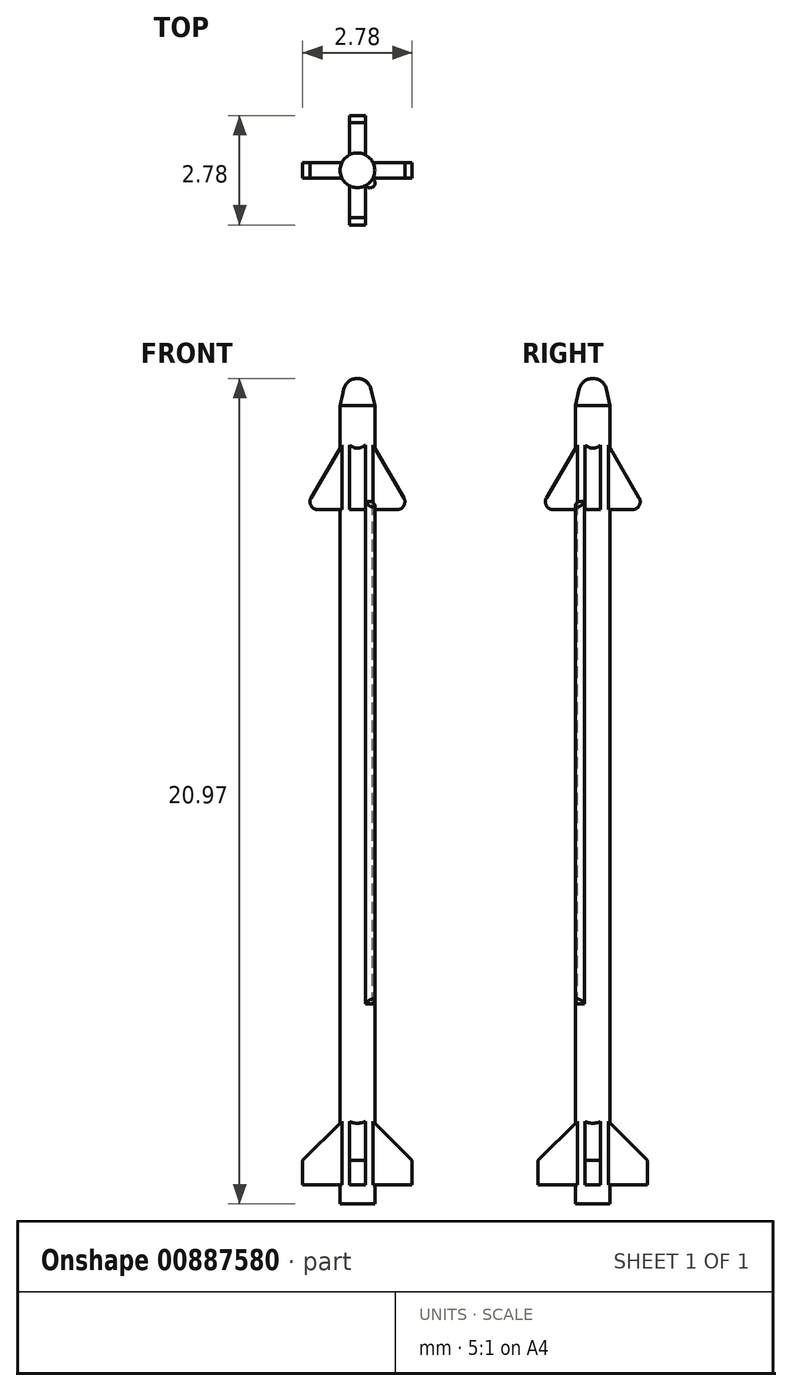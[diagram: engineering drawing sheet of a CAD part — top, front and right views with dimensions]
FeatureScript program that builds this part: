
annotation { "Feature Type Name" : "Feature", "Feature Type Description" : "" }
export const myFeature = defineFeature(function(context is Context, id is Id, definition is map)
    precondition{}
    {
        {
            var Q0;
            Q0=qCreatedBy(makeId("Front.planeOp"),FACE);
            var sketch = newSketch(context, id + "F0", { "sketchPlane" : qUnion([Q0])});
            skLineSegment(sketch, "E0", {"start": v(0, 0) * mm, "end": v(0, 20.97) * mm});
            skLineSegment(sketch, "E1", {"start": v(0.44, 20.28) * mm, "end": v(0.44, 0) * mm});
            skLineSegment(sketch, "E2", {"start": v(0.44, 0) * mm, "end": v(0, 0) * mm});
            skLineSegment(sketch, "E3", {"start": v(0, 20.97) * mm, "end": v(1.85, 20.97) * mm, "construction": true});
            skLineSegment(sketch, "E4", {"start": v(0.44, 20.28) * mm, "end": v(0.35, 20.7) * mm});
            skArc(sketch, "E5", {"start": v(0.35, 20.7) * mm, "mid": v(0.22, 20.9) * mm, "end": v(0, 20.97) * mm});
            skSolve(sketch);
        }
        {
            var Q0;
            Q0=qSketchRegion(id+"F0",true);
            var Q1;
            Q1=sQuery(id+"F0.wireOp",EDGE,"E0");
            revolve(context, id + "F1", {"surfaceOperationType" : NewSurfaceOperationType.NEW, "entities" : qUnion([Q0]), "axis" : qUnion([Q1]), "revolveType" : RevolveType.FULL});
        }
        {
            var Q0;
            Q0=qCreatedBy(makeId("Front.planeOp"),FACE);
            var sketch = newSketch(context, id + "F2", { "sketchPlane" : qUnion([Q0])});
            skLineSegment(sketch, "E6", {"start": v(0.25, 2.24) * mm, "end": v(-0.25, 2.24) * mm});
            skLineSegment(sketch, "E7", {"start": v(-1.39, 1.11) * mm, "end": v(-0.25, 2.24) * mm});
            skLineSegment(sketch, "E8", {"start": v(-1.39, 1.11) * mm, "end": v(-1.39, 0.49) * mm});
            skLineSegment(sketch, "E9", {"start": v(1.39, 0.49) * mm, "end": v(1.39, 1.11) * mm});
            skLineSegment(sketch, "E10", {"start": v(0.25, 2.24) * mm, "end": v(1.39, 1.11) * mm});
            skLineSegment(sketch, "E11", {"start": v(0, 0) * mm, "end": v(0, 2.24) * mm, "construction": true});
            skLineSegment(sketch, "E12", {"start": v(-0.44, 0.8) * mm, "end": v(-0.44, 4.16) * mm, "construction": true});
            skLineSegment(sketch, "E13.0", {"start": v(0.44, 20.28) * mm, "end": v(-0.44, 20.28) * mm});
            skLineSegment(sketch, "E14", {"start": v(0, 0) * mm, "end": v(0, 0.49) * mm, "construction": true});
            skLineSegment(sketch, "E15.0", {"start": v(0.44, 0) * mm, "end": v(-0.44, 0) * mm});
            skLineSegment(sketch, "E16", {"start": v(-1.35, 17.64) * mm, "end": v(1.35, 17.64) * mm});
            skLineSegment(sketch, "E17", {"start": v(-1.35, 17.64) * mm, "end": v(-0.25, 19.53) * mm});
            skLineSegment(sketch, "E18", {"start": v(-0.25, 19.53) * mm, "end": v(0.25, 19.53) * mm});
            skLineSegment(sketch, "E19", {"start": v(0.25, 19.53) * mm, "end": v(1.35, 17.64) * mm});
            skLineSegment(sketch, "E20", {"start": v(0, 19.53) * mm, "end": v(0, 17.64) * mm, "construction": true});
            skLineSegment(sketch, "E21", {"start": v(-1.39, 0.49) * mm, "end": v(1.39, 0.49) * mm});
            skPoint(sketch, "E22", {"position": v(-0.44, 2.05) * mm});
            skLineSegment(sketch, "E23", {"start": v(-0.44, 20.28) * mm, "end": v(-0.44, 16.68) * mm, "construction": true});
            skPoint(sketch, "E24", {"position": v(-0.44, 19.2) * mm});
            skSolve(sketch);
        }
        {
            var Q0;
            Q0=qSketchRegion(id+"F2",true);
            extrude(context, id + "F3", {"entities" : qUnion([Q0]), "operationType" : NewBodyOperationType.ADD, "depth" : .4 * mm, "offsetDistance" : 25 * mm, "symmetric" : true});
        }
        {
            var Q0;
            Q0=makeQuery(id+"F3.opExtrude","SWEPT_EDGE",EDGE,{"disambiguationData":[OSD([sQuery(id+"F2.wireOp",EDGE,"IMAepUiN-4dFO-ApNK-NmcL-y1ty9Cx0r7KA"),sQuery(id+"F2.wireOp",EDGE,"E16")])]});
            var Q1;
            Q1=makeQuery(id+"F3.opExtrude","SWEPT_EDGE",EDGE,{"disambiguationData":[OSD([sQuery(id+"F2.wireOp",EDGE,"Mpjs0J2t-wY67-a0AX-eRwJ-QufGG5zaKpuO"),sQuery(id+"F2.wireOp",EDGE,"E16")])]});
            fillet(context, id + "F4", {"entities" : qUnion([Q0, Q1]), "radius" : .2 * mm, "tangentPropagation" : true, "allowEdgeOverflow" : false});
        }
        {
            var Q0;
            Q0=makeQuery(id+"F1.opRevolve","SWEPT_BODY",BODY,{"disambiguationData":[OSD([sQuery(id+"F0.wireOp",EDGE,"E0"),sQuery(id+"F0.wireOp",EDGE,"E1"),sQuery(id+"F0.wireOp",EDGE,"E2"),sQuery(id+"F0.wireOp",EDGE,"m1K1lCZm-MTc8-Btmt-IA6e-LtdyprMEJuD3")])]});
            var Q1;
            Q1=makeQuery(id+"F1.opRevolve","SWEPT_FACE",FACE,{"disambiguationData":[OSD([sQuery(id+"F0.wireOp",EDGE,"E1")])]});
            circularPattern(context, id + "F5", {"entities" : qUnion([Q0]), "axis" : qUnion([Q1]), "angle" : 360 * degree, "instanceCount" : 4, "equalSpace" : true, "computeTransformsWithoutBuiltin" : true});
        }
        {
            var Q0;
            {var subQ2=sQuery(id+"F2.wireOp",EDGE,"E17");var subQ3=sQuery(id+"F2.wireOp",EDGE,"E16");Q0=makeQuery(id+"F5.opPattern","COPY",FACE,{"derivedFrom":makeQuery(id+"F3.boolean.opBoolean","SPLIT",FACE,{"disambiguationData":[TD([makeQuery(id+"F3.opExtrude","SWEPT_FACE",FACE,{"disambiguationData":[OSD([subQ2])]})])],"derivedFrom":makeQuery(id+"F3.opExtrude","SWEPT_FACE",FACE,{"disambiguationData":[OSD([subQ3])]})}),"instanceName":"1"});}
            var sketch = newSketch(context, id + "F6", { "sketchPlane" : qUnion([Q0])});
            skCircle(sketch, "E25.0.0", {"center": v(0, 0) * mm, "radius": 0.44 * mm});
            skArc(sketch, "E26", {"start": v(0.41, 0.23) * mm, "mid": v(0.41, 0.41) * mm, "end": v(0.23, 0.41) * mm});
            skLineSegment(sketch, "E27", {"start": v(0.23, 0.41) * mm, "end": v(0.2, 0.38) * mm});
            skLineSegment(sketch, "E28", {"start": v(0.2, 0.38) * mm, "end": v(0.38, 0.2) * mm});
            skLineSegment(sketch, "E29", {"start": v(0.38, 0.2) * mm, "end": v(0.41, 0.23) * mm});
            skLineSegment(sketch, "E30", {"start": v(0.3, 0.3) * mm, "end": v(0, 0) * mm, "construction": true});
            skLineSegment(sketch, "E31", {"start": v(0, 0) * mm, "end": v(0.17, 0) * mm, "construction": true});
            skSolve(sketch);
        }
        {
            var Q0;
            Q0 = qSketchRegion(id + "F6", true);
            extrude(context, id + "F7", {"entities" : qUnion([Q0]), "operationType" : NewBodyOperationType.ADD, "depth" : (1780 / 144) * mm, "offsetDistance" : 25 * mm});
        }
        {
            var Q0;
            {var subQ0=makeQuery(id+"F1.opRevolve","SWEPT_FACE",FACE,{"disambiguationData":[OSD([sQuery(id+"F0.wireOp",EDGE,"E1")])]});Q0=makeQuery(id+"F7.boolean.opBoolean","INTERSECT",EDGE,{"derivedFrom":[subQ0,makeQuery(id+"F5.opPattern","COPY",FACE,{"derivedFrom":subQ0,"instanceName":"1"}),makeQuery(id+"F5.opPattern","COPY",FACE,{"derivedFrom":subQ0,"instanceName":"2"}),makeQuery(id+"F5.opPattern","COPY",FACE,{"derivedFrom":subQ0,"instanceName":"3"}),makeQuery(id+"F7.opExtrude","CAP_FACE",FACE,{"disambiguationData":[OSD([sQuery(id+"F6.wireOp",EDGE,"E25.0.0"),sQuery(id+"F6.wireOp",EDGE,"E26"),sQuery(id+"F6.wireOp",EDGE,"E27"),sQuery(id+"F6.wireOp",EDGE,"E29")])],"isStart":false})]});}
            var Q1;
            {var subQ0=makeQuery(id+"F1.opRevolve","SWEPT_FACE",FACE,{"disambiguationData":[OSD([sQuery(id+"F0.wireOp",EDGE,"E1")])]});Q1=makeQuery(id+"F7.boolean.opBoolean","INTERSECT",EDGE,{"derivedFrom":[subQ0,makeQuery(id+"F5.opPattern","COPY",FACE,{"derivedFrom":subQ0,"instanceName":"1"}),makeQuery(id+"F5.opPattern","COPY",FACE,{"derivedFrom":subQ0,"instanceName":"2"}),makeQuery(id+"F5.opPattern","COPY",FACE,{"derivedFrom":subQ0,"instanceName":"3"}),makeQuery(id+"F7.opExtrude","CAP_FACE",FACE,{"disambiguationData":[OSD([sQuery(id+"F6.wireOp",EDGE,"E25.0.0"),sQuery(id+"F6.wireOp",EDGE,"E26"),sQuery(id+"F6.wireOp",EDGE,"E27"),sQuery(id+"F6.wireOp",EDGE,"E29")])],"isStart":true})]});}
            chamfer(context, id + "F8", {"entities" : qUnion([Q0, Q1]), "width" : .2 * mm, "tangentPropagation" : true});
        }
    });
